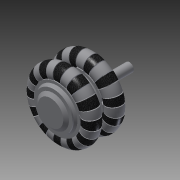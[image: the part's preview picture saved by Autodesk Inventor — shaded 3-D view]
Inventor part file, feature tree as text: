
AUTODESK INVENTOR PART (.ipt)
format: ipt  version: 2015 (Build 190159000, 159)  size: 1,512,960 bytes
history: native  units: in
note: dims shown in document units (in); Inventor stores cm internally (conversion verified against a paired STEP export)
features: sketch x4, other x3, extrude x1
ambient origin geometry x8: Origin, YZ Plane, XZ Plane, XY Plane, X Axis, Y Axis, Z Axis, Center Point
bodies: Solid1 (feature_tree), Solid2 (feature_tree)
feature tree (8):
  other  "omniWheelSet.ipt"
  extrude  "Extrusion1"  Depth=0.1181in TaperAngle=0.0deg
  sketch  "Sketch1"  dims[d0=1.9685in d1=0.1181in d2=0.0in]
  other  "Solid1::omniWheelSet.ipt"
  other  "TaggingFeature1"
  sketch  "Sketch3"  dims[d4=3.937in]
  sketch  "Sketch5"
  sketch  "Sketch15"
